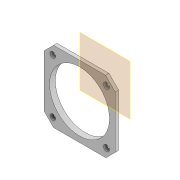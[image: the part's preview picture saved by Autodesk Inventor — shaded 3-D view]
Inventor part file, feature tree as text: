
AUTODESK INVENTOR PART (.ipt)
format: ipt  version: 2022 (Build 260153000, 153)  size: 154,112 bytes
history: native  units: mm
features: extrude x2, sketch x2, plane x1
ambient origin geometry x8: Origin, YZ Plane, XZ Plane, XY Plane, X Axis, Y Axis, Z Axis, Center Point
bodies: Volumenkörper1 (feature_tree)
feature tree (5):
  plane  "Arbeitsebene1"
  extrude  "Extrusion1"  Depth=1.5mm
  extrude  "Extrusion2"  [1 undecoded]
  sketch  "Skizze1"  dims[d0=1.5mm d1=0.0mm d2=28.0mm]
  sketch  "Skizze2"  dims[d3=1.0mm d4=0.0mm]
note: 1 required parameter value undecoded (feature->parameter linkage not recoverable at this tier; creation-order binding heuristic only, values carry confidence <= 0.55)
